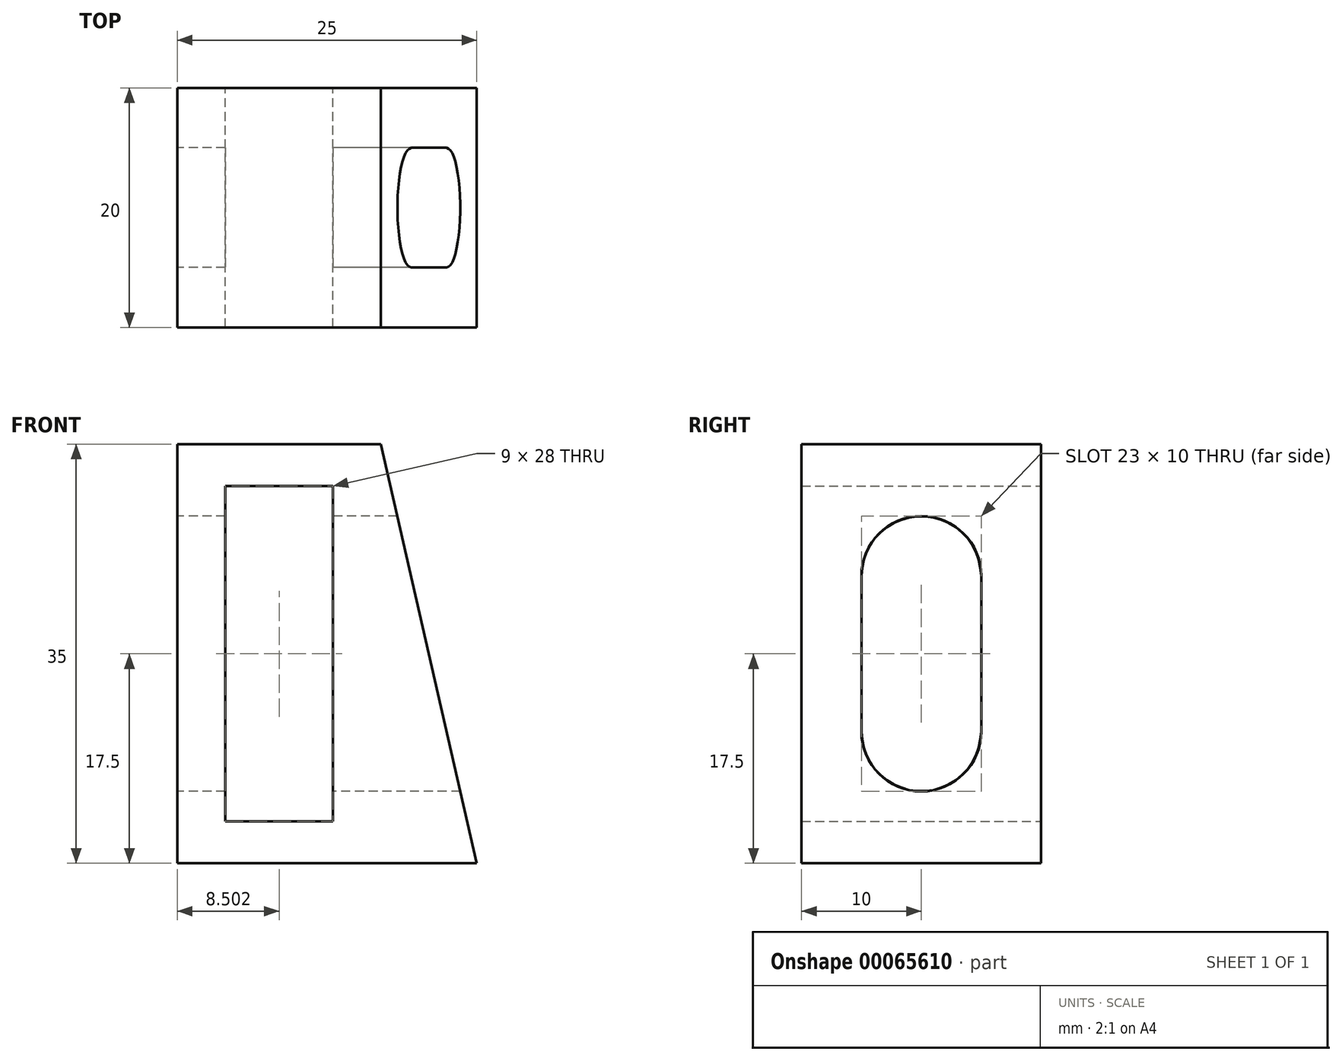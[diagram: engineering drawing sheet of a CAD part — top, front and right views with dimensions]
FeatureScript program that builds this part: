
annotation { "Feature Type Name" : "Feature", "Feature Type Description" : "" }
export const myFeature = defineFeature(function(context is Context, id is Id, definition is map)
    precondition{}
    {
        {
            var Q0;
            Q0=qCreatedBy(makeId("Front.planeOp"),FACE);
            var sketch = newSketch(context, id + "F0", { "sketchPlane" : qUnion([Q0])});
            skLineSegment(sketch, "E0.bottom", {"start": v(-26.63, 0) * mm, "end": v(-1.63, 0) * mm});
            skLineSegment(sketch, "E0.top", {"start": v(-26.63, 35) * mm, "end": v(-1.63, 35) * mm});
            skLineSegment(sketch, "E0.left", {"start": v(-26.63, 0) * mm, "end": v(-26.63, 35) * mm});
            skLineSegment(sketch, "E0.right", {"start": v(-1.63, 0) * mm, "end": v(-1.63, 35) * mm});
            skSolve(sketch);
        }
        {
            var Q0;
            Q0=makeQuery(id+"F0.imprint","IMPRINT",FACE,{"disambiguationData":[TD([[makeQuery(id+"F0.imprint","IMPRINT",EDGE,{"derivedFrom":sQuery(id+"F0.wireOp",EDGE,"E0.bottom")}),1.0]])]});
            extrude(context, id + "F1", {"entities" : qUnion([Q0]), "endBound" : BoundingType.SYMMETRIC, "depth" : 20 * mm});
        }
        {
            var Q0;
            Q0=makeQuery(id+"F1.opExtrude","SWEPT_EDGE",EDGE,{"disambiguationData":[OSD([sQuery(id+"F0.wireOp",EDGE,"E0.top"),sQuery(id+"F0.wireOp",EDGE,"E0.right")])]});
            chamfer(context, id + "F2", {"entities" : qUnion([Q0]), "chamferType" : ChamferType.TWO_OFFSETS, "width1" : 8 * mm, "oppositeDirection" : false, "width2" : 35 * mm, "tangentPropagation" : true});
        }
        {
            var Q0;
            Q0=makeQuery(id+"F1.opExtrude","CAP_FACE",FACE,{"disambiguationData":[OSD([sQuery(id+"F0.wireOp",EDGE,"E0.bottom"),sQuery(id+"F0.wireOp",EDGE,"E0.top"),sQuery(id+"F0.wireOp",EDGE,"E0.left"),sQuery(id+"F0.wireOp",EDGE,"E0.right")])],"isStart":true});
            var sketch = newSketch(context, id + "F3", { "sketchPlane" : qUnion([Q0])});
            skLineSegment(sketch, "E1.bottom", {"start": v(13.63, 31.5) * mm, "end": v(22.63, 31.5) * mm});
            skLineSegment(sketch, "E1.top", {"start": v(13.63, 3.5) * mm, "end": v(22.63, 3.5) * mm});
            skLineSegment(sketch, "E1.left", {"start": v(13.63, 31.5) * mm, "end": v(13.63, 3.5) * mm});
            skLineSegment(sketch, "E1.right", {"start": v(22.63, 31.5) * mm, "end": v(22.63, 3.5) * mm});
            skSolve(sketch);
        }
        {
            var Q0;
            Q0=makeQuery(id+"F3.imprint","IMPRINT",FACE,{"disambiguationData":[TD([[makeQuery(id+"F3.imprint","IMPRINT",EDGE,{"derivedFrom":sQuery(id+"F3.wireOp",EDGE,"E1.bottom")}),-1.0]])]});
            extrude(context, id + "F4", {"entities" : qUnion([Q0]), "operationType" : NewBodyOperationType.REMOVE, "oppositeDirection" : true, "depth" : 33.36 * mm});
        }
        {
            var Q0;
            Q0=makeQuery(id+"F1.opExtrude","SWEPT_FACE",FACE,{"disambiguationData":[OSD([sQuery(id+"F0.wireOp",EDGE,"E0.left")])]});
            var sketch = newSketch(context, id + "F5", { "sketchPlane" : qUnion([Q0])});
            skLineSegment(sketch, "E2.rect.bottom", {"start": v(-5, 24) * mm, "end": v(5, 24) * mm});
            skLineSegment(sketch, "E2.rect.top", {"start": v(-5, 11) * mm, "end": v(5, 11) * mm});
            skLineSegment(sketch, "E2.rect.left", {"start": v(-5, 24) * mm, "end": v(-5, 11) * mm});
            skLineSegment(sketch, "E2.rect.right", {"start": v(5, 24) * mm, "end": v(5, 11) * mm});
            skPoint(sketch, "E2.rect.middle", {"position": v(0, 17.5) * mm});
            skArc(sketch, "E3", {"start": v(5, 24) * mm, "mid": v(0, 29) * mm, "end": v(-5, 24) * mm});
            skArc(sketch, "E4", {"start": v(-5, 11) * mm, "mid": v(0, 6) * mm, "end": v(5, 11) * mm});
            skSolve(sketch);
        }
        {
            var Q0;
            Q0=makeQuery(id+"F5.imprint","IMPRINT",FACE,{"disambiguationData":[TD([[makeQuery(id+"F5.imprint","IMPRINT",EDGE,{"derivedFrom":sQuery(id+"F5.wireOp",EDGE,"E2.rect.bottom")}),1.0]])]});
            var Q1;
            Q1=makeQuery(id+"F5.imprint","IMPRINT",FACE,{"disambiguationData":[TD([[makeQuery(id+"F5.imprint","IMPRINT",EDGE,{"derivedFrom":sQuery(id+"F5.wireOp",EDGE,"E2.rect.bottom")}),-1.0]])]});
            var Q2;
            Q2=makeQuery(id+"F5.imprint","IMPRINT",FACE,{"disambiguationData":[TD([[makeQuery(id+"F5.imprint","IMPRINT",EDGE,{"derivedFrom":sQuery(id+"F5.wireOp",EDGE,"E2.rect.top")}),-1.0]])]});
            extrude(context, id + "F6", {"entities" : qUnion([Q0, Q1, Q2]), "operationType" : NewBodyOperationType.REMOVE, "oppositeDirection" : true, "depth" : 25 * mm});
        }
    });
